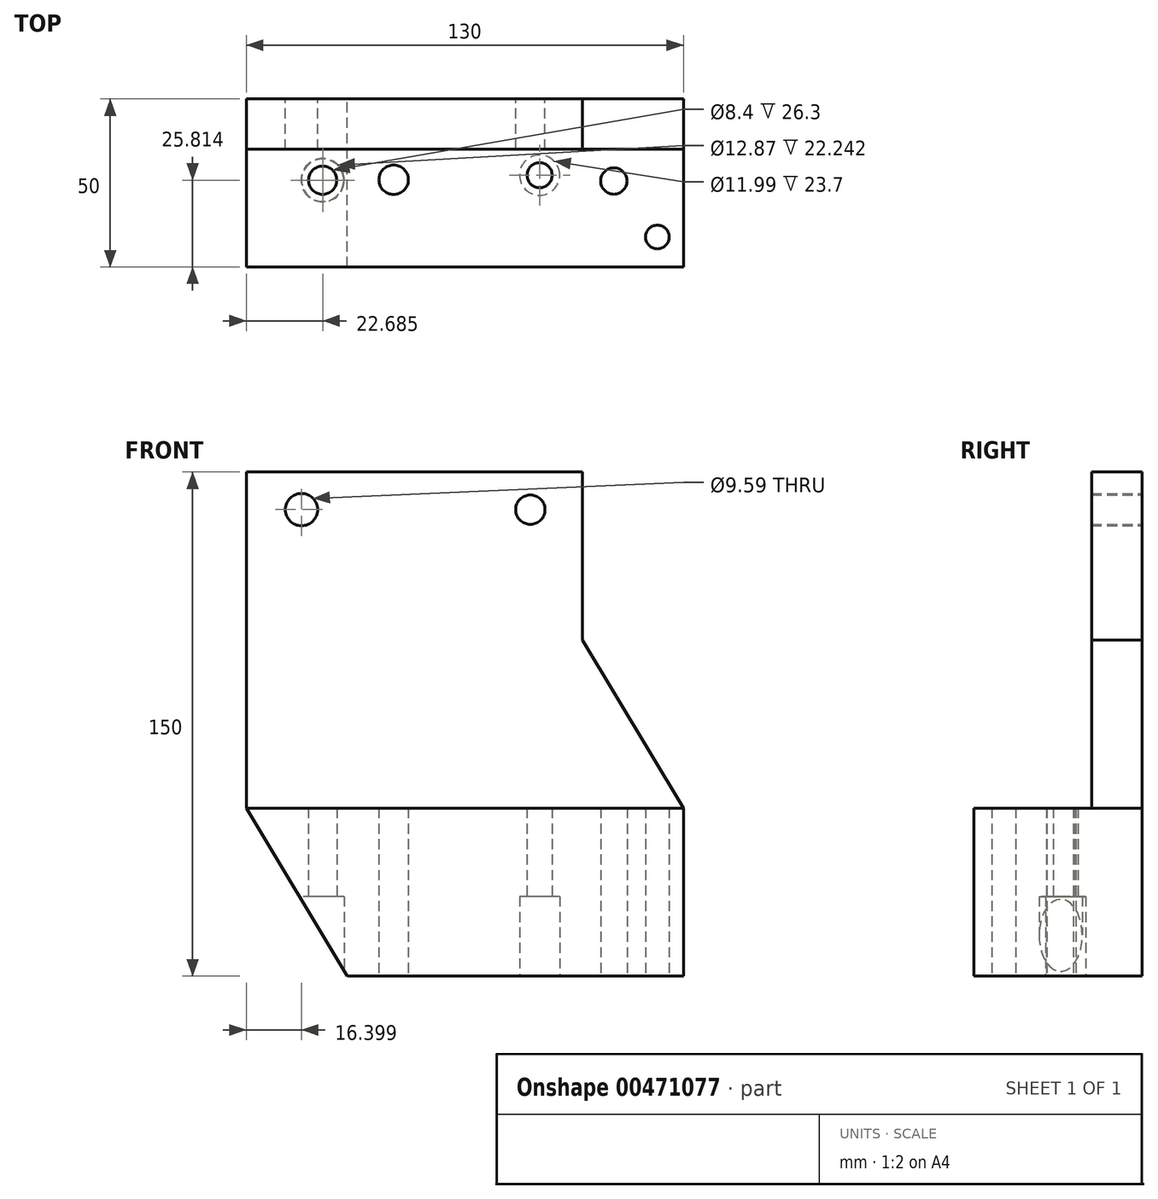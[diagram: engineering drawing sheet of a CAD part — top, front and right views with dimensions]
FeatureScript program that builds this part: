
annotation { "Feature Type Name" : "Feature", "Feature Type Description" : "" }
export const myFeature = defineFeature(function(context is Context, id is Id, definition is map)
    precondition{}
    {
        {
            var Q0;
            Q0=qCreatedBy(makeId("Front.planeOp"),FACE);
            var sketch = newSketch(context, id + "F0", { "sketchPlane" : qUnion([Q0])});
            skLineSegment(sketch, "E0.bottom", {"start": v(0, 0) * mm, "end": v(-100, 0) * mm});
            skLineSegment(sketch, "E0.top", {"start": v(0, 50) * mm, "end": v(-100, 50) * mm});
            skLineSegment(sketch, "E0.left", {"start": v(0, 0) * mm, "end": v(0, 50) * mm});
            skLineSegment(sketch, "E0.right", {"start": v(-100, 0) * mm, "end": v(-100, 50) * mm});
            skLineSegment(sketch, "E1.bottom", {"start": v(-30, 50) * mm, "end": v(-130, 50) * mm});
            skLineSegment(sketch, "E1.top", {"start": v(-30, 150) * mm, "end": v(-130, 150) * mm});
            skLineSegment(sketch, "E1.left", {"start": v(-30, 50) * mm, "end": v(-30, 150) * mm});
            skLineSegment(sketch, "E1.right", {"start": v(-130, 50) * mm, "end": v(-130, 150) * mm});
            skLineSegment(sketch, "E2", {"start": v(-130, 50) * mm, "end": v(-100, 0) * mm});
            skLineSegment(sketch, "E3", {"start": v(0, 50) * mm, "end": v(-30, 100) * mm});
            skCircle(sketch, "E4", {"center": v(-113.6, 138.8) * mm, "radius": 4.8 * mm});
            skCircle(sketch, "E5", {"center": v(-45.53, 138.8) * mm, "radius": 4.37 * mm});
            skSolve(sketch);
        }
        {
            var Q0;
            {var subQ4=sQuery(id+"F0.wireOp",EDGE,"E1.top");Q0=makeQuery(id+"F0.imprint","IMPRINT",FACE,{"disambiguationData":[TD([[makeQuery(id+"F0.imprint","IMPRINT",EDGE,{"derivedFrom":subQ4}),1.0]])]});}
            var Q1;
            {var subQ0=sQuery(id+"F0.wireOp",EDGE,"E0.top");Q1=makeQuery(id+"F0.imprint","IMPRINT",FACE,{"disambiguationData":[TD([[makeQuery(id+"F0.imprint","IMPRINT",EDGE,{"derivedFrom":subQ0}),-1.0]])]});}
            extrude(context, id + "F1", {"entities" : qUnion([Q0, Q1]), "depth" : 15 * mm});
        }
        {
            var Q0;
            {var subQ0=sQuery(id+"F0.wireOp",EDGE,"E0.right");Q0=makeQuery(id+"F0.imprint","IMPRINT",FACE,{"disambiguationData":[TD([[makeQuery(id+"F0.imprint","IMPRINT",EDGE,{"derivedFrom":subQ0}),1.0]])]});}
            var Q1;
            Q1=makeQuery(id+"F0.imprint","IMPRINT",FACE,{"disambiguationData":[TD([[makeQuery(id+"F0.imprint","IMPRINT",EDGE,{"derivedFrom":sQuery(id+"F0.wireOp",EDGE,"E0.bottom")}),-1.0]])]});
            extrude(context, id + "F2", {"entities" : qUnion([Q0, Q1]), "operationType" : NewBodyOperationType.ADD, "depth" : 50 * mm});
        }
        {
            var Q0;
            Q0=qCreatedBy(makeId("Top.planeOp"),FACE);
            var sketch = newSketch(context, id + "F3", { "sketchPlane" : qUnion([Q0])});
            skCircle(sketch, "E6", {"center": v(-7.72, -41.1) * mm, "radius": 3.53 * mm});
            skCircle(sketch, "E7", {"center": v(-20.69, -24.42) * mm, "radius": 3.93 * mm});
            skCircle(sketch, "E8", {"center": v(-107.32, -24.19) * mm, "radius": 4.2 * mm});
            skCircle(sketch, "E9", {"center": v(-42.76, -22.69) * mm, "radius": 3.72 * mm});
            skCircle(sketch, "E10", {"center": v(-86.2, -24.05) * mm, "radius": 4.37 * mm});
            skCircle(sketch, "E11", {"center": v(-107.32, -24.19) * mm, "radius": 6.44 * mm});
            skCircle(sketch, "E12", {"center": v(-42.76, -22.69) * mm, "radius": 6 * mm});
            skSolve(sketch);
        }
        {
            var Q0;
            Q0=makeQuery(id+"F3.imprint","IMPRINT",FACE,{"disambiguationData":[TD([[makeQuery(id+"F3.imprint","IMPRINT",EDGE,{"derivedFrom":sQuery(id+"F3.wireOp",EDGE,"E7")}),1.0]])]});
            var Q1;
            Q1=makeQuery(id+"F3.imprint","IMPRINT",FACE,{"disambiguationData":[TD([[makeQuery(id+"F3.imprint","IMPRINT",EDGE,{"derivedFrom":sQuery(id+"F3.wireOp",EDGE,"E10")}),1.0]])]});
            var Q2;
            Q2=makeQuery(id+"F3.imprint","IMPRINT",FACE,{"disambiguationData":[TD([[makeQuery(id+"F3.imprint","IMPRINT",EDGE,{"derivedFrom":sQuery(id+"F3.wireOp",EDGE,"E8")}),1.0]])]});
            var Q3;
            Q3=makeQuery(id+"F3.imprint","IMPRINT",FACE,{"disambiguationData":[TD([[makeQuery(id+"F3.imprint","IMPRINT",EDGE,{"derivedFrom":sQuery(id+"F3.wireOp",EDGE,"E9")}),1.0]])]});
            var Q4;
            Q4=makeQuery(id+"F3.imprint","IMPRINT",FACE,{"disambiguationData":[TD([[makeQuery(id+"F3.imprint","IMPRINT",EDGE,{"derivedFrom":sQuery(id+"F3.wireOp",EDGE,"E6")}),1.0]])]});
            extrude(context, id + "F4", {"entities" : qUnion([Q0, Q1, Q2, Q3, Q4]), "operationType" : NewBodyOperationType.REMOVE, "depth" : 69 * mm});
        }
        {
            var Q0;
            Q0=makeQuery(id+"F3.imprint","IMPRINT",FACE,{"disambiguationData":[TD([[makeQuery(id+"F3.imprint","IMPRINT",EDGE,{"derivedFrom":sQuery(id+"F3.wireOp",EDGE,"E8")}),-1.0]])]});
            var Q1;
            Q1=makeQuery(id+"F3.imprint","IMPRINT",FACE,{"disambiguationData":[TD([[makeQuery(id+"F3.imprint","IMPRINT",EDGE,{"derivedFrom":sQuery(id+"F3.wireOp",EDGE,"E9")}),-1.0]])]});
            extrude(context, id + "F5", {"entities" : qUnion([Q0, Q1]), "operationType" : NewBodyOperationType.REMOVE, "depth" : 23.7 * mm});
        }
    });
